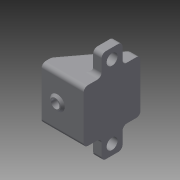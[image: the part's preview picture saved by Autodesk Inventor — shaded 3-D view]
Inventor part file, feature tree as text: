
AUTODESK INVENTOR PART (.ipt)
format: ipt  version: 2015 (Build 190159000, 159)  size: 166,400 bytes
history: native  units: in
note: dims shown in document units (in); Inventor stores cm internally (conversion verified against a paired STEP export)
features: sketch x8, other x3, plane x2
ambient origin geometry x8: Origin, YZ Plane, XZ Plane, XY Plane, X Axis, Y Axis, Z Axis, Center Point
bodies: Solid1 (feature_tree)
feature tree (13):
  other  "holder1.ipt"
  other  "Solid1::holder1.ipt"
  other  "TaggingFeature1"
  sketch  "Sketch1"  dims[d0=0.3937in]
  sketch  "Sketch2"
  sketch  "Sketch3"
  sketch  "Sketch4"
  sketch  "Sketch5"
  sketch  "Sketch6"
  sketch  "Sketch7"
  sketch  "Sketch8"
  plane  "Work Plane1"
  plane  "Work Plane2"
